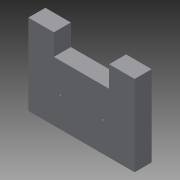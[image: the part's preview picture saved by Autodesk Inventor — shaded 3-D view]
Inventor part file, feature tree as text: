
AUTODESK INVENTOR PART (.ipt)
format: ipt  version: 2015 (Build 190159000, 159)  size: 81,920 bytes
history: native  units: mm
features: extrude x1, sketch x1
ambient origin geometry x8: Origin, YZ Plane, XZ Plane, XY Plane, X Axis, Y Axis, Z Axis, Center Point
bodies: Solid1 (feature_tree)
feature tree (2):
  extrude  "Extrusion1"  Depth=9.5mm
  sketch  "Sketch1"  dims[d0=12.5mm d1=9.5mm d2=3.0mm d3=2.5mm d4=6.5mm d7=0.2mm d9=0.2mm d10=2.0mm d11=0.0mm]
